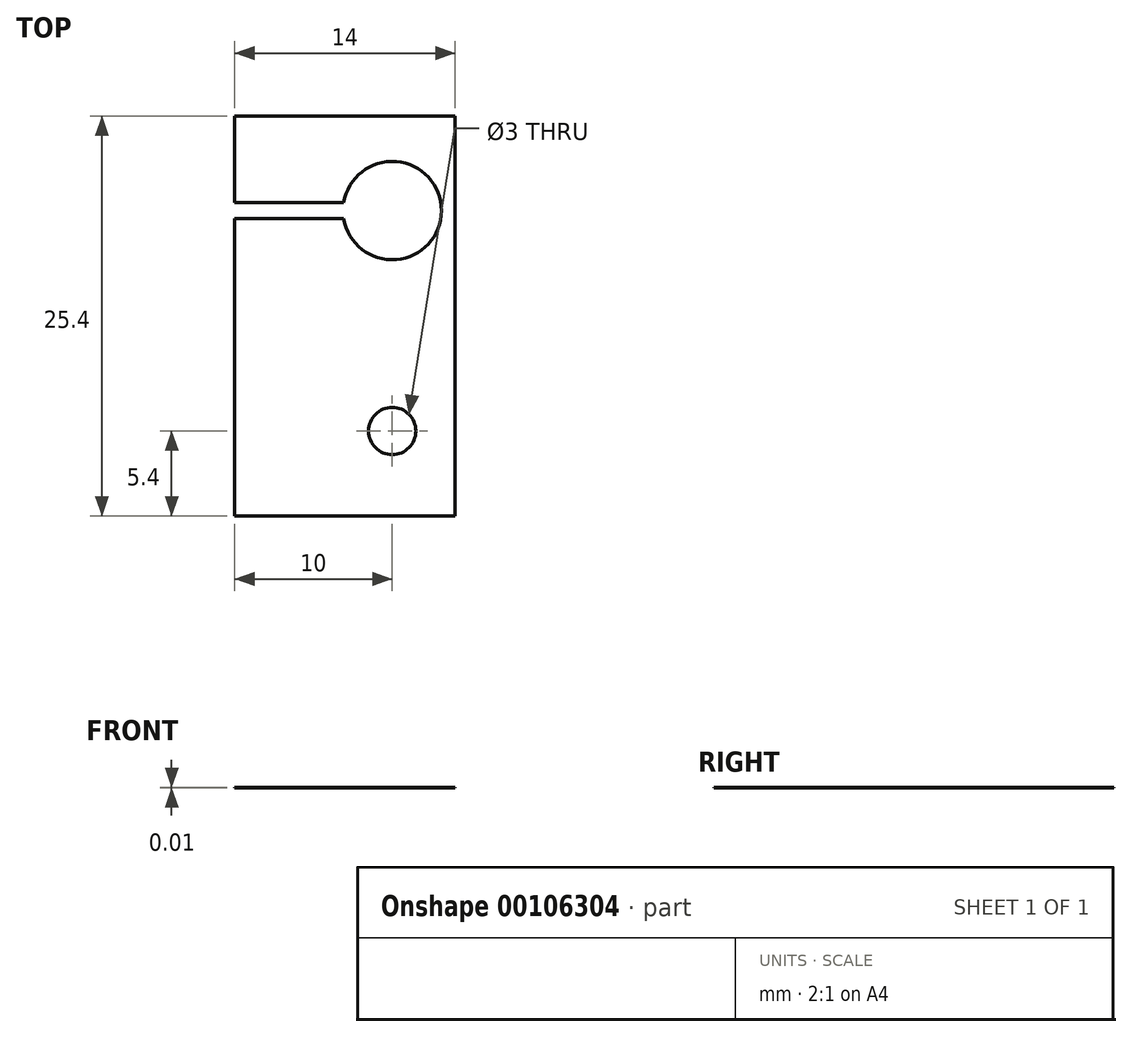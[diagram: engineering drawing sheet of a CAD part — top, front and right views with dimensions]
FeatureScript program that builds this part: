
annotation { "Feature Type Name" : "Feature", "Feature Type Description" : "" }
export const myFeature = defineFeature(function(context is Context, id is Id, definition is map)
    precondition{}
    {
        {
            var Q0;
            Q0=qCreatedBy(makeId("Top.planeOp"),FACE);
            var sketch = newSketch(context, id + "F0", { "sketchPlane" : qUnion([Q0])});
            skLineSegment(sketch, "E0.bottom", {"start": v(7, -12.7) * mm, "end": v(-7, -12.7) * mm});
            skLineSegment(sketch, "E0.top", {"start": v(7, 12.7) * mm, "end": v(-7, 12.7) * mm});
            skLineSegment(sketch, "E0.left", {"start": v(7, -12.7) * mm, "end": v(7, 12.7) * mm});
            skLineSegment(sketch, "E0.right", {"start": v(-7, -12.7) * mm, "end": v(-7, 6.2) * mm});
            skPoint(sketch, "E0.middle", {"position": v(0, 0) * mm});
            skArc(sketch, "E1", {"start": v(-0.08, 6.2) * mm, "mid": v(6.12, 6.7) * mm, "end": v(-0.08, 7.2) * mm});
            skCircle(sketch, "E2", {"center": v(3, -7.3) * mm, "radius": 1.5 * mm});
            skLineSegment(sketch, "E3.bottom", {"start": v(-4.5, 12.7) * mm, "end": v(-1.5, 12.7) * mm, "construction": true});
            skLineSegment(sketch, "E3.top", {"start": v(-4.5, -12.7) * mm, "end": v(-1.5, -12.7) * mm, "construction": true});
            skLineSegment(sketch, "E3.left", {"start": v(-4.5, 12.7) * mm, "end": v(-4.5, -12.7) * mm, "construction": true});
            skLineSegment(sketch, "E3.right", {"start": v(-1.5, 12.7) * mm, "end": v(-1.5, -12.7) * mm, "construction": true});
            skLineSegment(sketch, "E4.bottom", {"start": v(-7, 7.2) * mm, "end": v(-0.08, 7.2) * mm});
            skLineSegment(sketch, "E4.top", {"start": v(-7, 6.2) * mm, "end": v(-0.08, 6.2) * mm});
            skLineSegment(sketch, "E5.trimOffspring", {"start": v(-7, 7.2) * mm, "end": v(-7, 12.7) * mm});
            skSolve(sketch);
        }
        {
            var Q0;
            Q0=qSketchRegion(id+"F0",true);
            extrude(context, id + "F1", {"entities" : qUnion([Q0]), "depth" : 3 / 203.2 * mm});
        }
        {
            var Q0;
            Q0=makeQuery(id+"F1.opExtrude","SWEPT_FACE",FACE,{"disambiguationData":[OSD([sQuery(id+"F0.wireOp",EDGE,"E0.top")])]});
            var sketch = newSketch(context, id + "F2", { "sketchPlane" : qUnion([Q0])});
            skCircle(sketch, "E6", {"center": v(3.54, 4.76) * mm, "radius": 1.25 * mm});
            skLineSegment(sketch, "E7", {"start": v(7, 4.76) * mm, "end": v(0.08, 4.76) * mm, "construction": true});
            skSolve(sketch);
        }
        {
            var Q0;
            Q0 = qSketchRegion(id + "F2", true);
            extrude(context, id + "F3", {"entities" : qUnion([Q0]), "operationType" : NewBodyOperationType.REMOVE, "endBound" : BoundingType.THROUGH_ALL, "oppositeDirection" : true, "depth" : 25 * mm});
        }
    });
